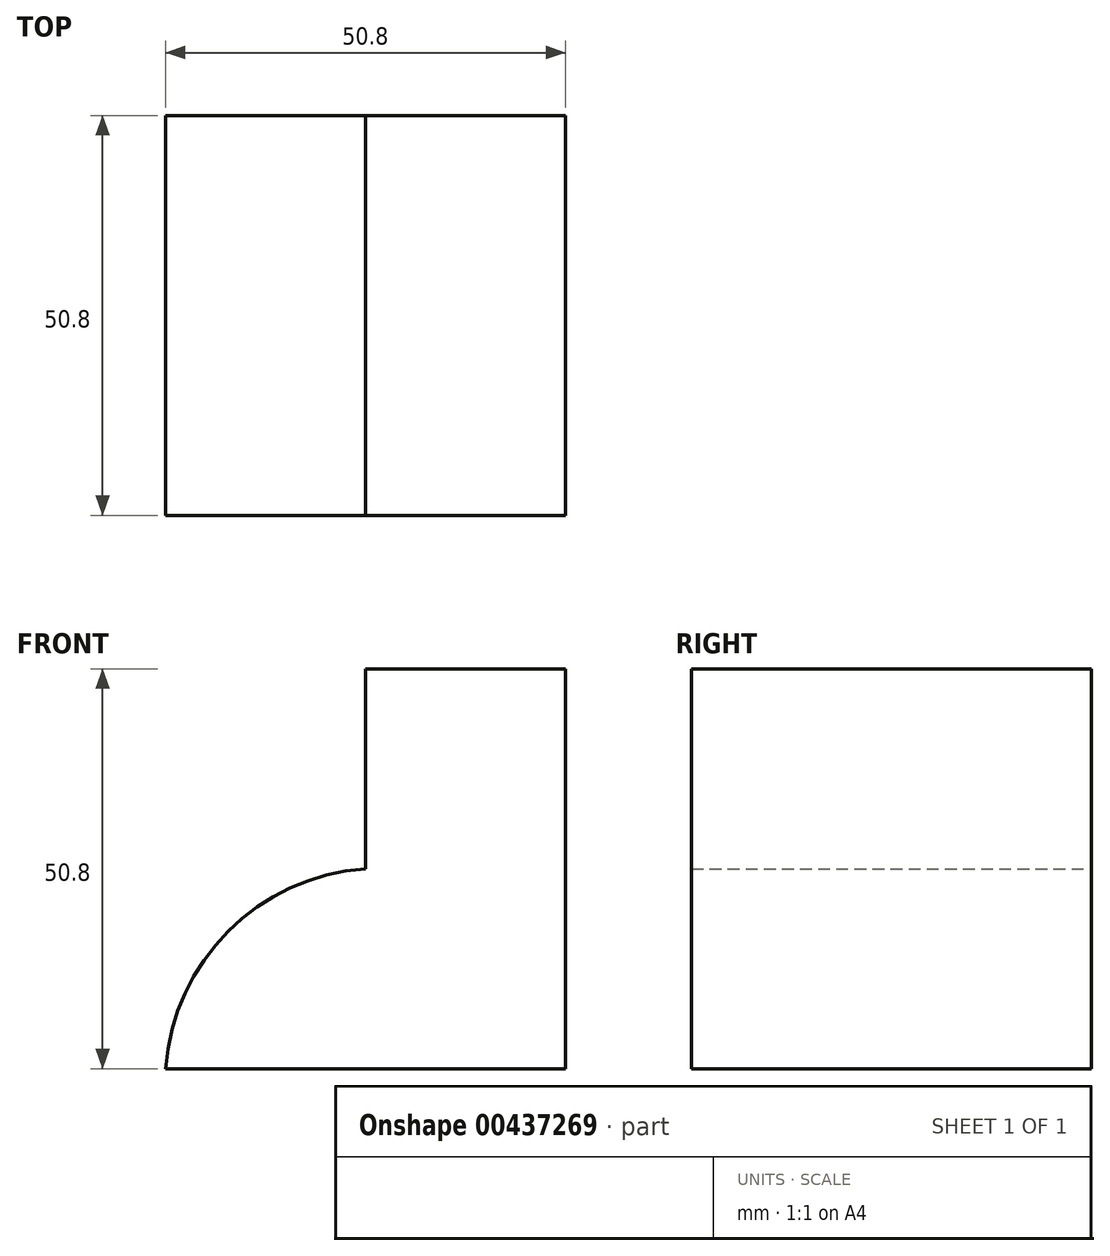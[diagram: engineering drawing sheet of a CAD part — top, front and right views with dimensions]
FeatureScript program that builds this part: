
annotation { "Feature Type Name" : "Feature", "Feature Type Description" : "" }
export const myFeature = defineFeature(function(context is Context, id is Id, definition is map)
    precondition{}
    {
        {
            var Q0;
            Q0=qCreatedBy(makeId("Front.planeOp"),FACE);
            var sketch = newSketch(context, id + "F0", { "sketchPlane" : qUnion([Q0])});
            skLineSegment(sketch, "E0", {"start": v(0, 0) * mm, "end": v(0, 50.8) * mm});
            skLineSegment(sketch, "E1", {"start": v(0, 50.8) * mm, "end": v(0, 0) * mm});
            skLineSegment(sketch, "E2", {"start": v(0, 0) * mm, "end": v(-50.8, 0) * mm});
            skLineSegment(sketch, "E3", {"start": v(0, 50.8) * mm, "end": v(-25.4, 50.8) * mm});
            skLineSegment(sketch, "E4", {"start": v(-25.4, 50.8) * mm, "end": v(-25.4, 25.4) * mm});
            skArc(sketch, "E5", {"start": v(-25.4, 25.4) * mm, "mid": v(-42.85, 17.45) * mm, "end": v(-50.8, 0) * mm});
            skSolve(sketch);
        }
        {
            var Q0;
            Q0 = qSketchRegion(id + "F0", true);
            extrude(context, id + "F1", {"entities" : qUnion([Q0]), "depth" : 50.8 * mm});
        }
    });
